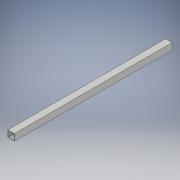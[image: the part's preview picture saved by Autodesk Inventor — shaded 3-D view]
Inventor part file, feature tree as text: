
AUTODESK INVENTOR PART (.ipt)
format: ipt  version: 2017 SP1 (Build 210196100, 196)  size: 98,304 bytes
history: native  units: in
note: dims shown in document units (in); Inventor stores cm internally (conversion verified against a paired STEP export)
features: extrude x1, sketch x1
ambient origin geometry x8: Origin, YZ Plane, XZ Plane, XY Plane, X Axis, Y Axis, Z Axis, Center Point
bodies: Solid1 (feature_tree)
feature tree (2):
  extrude  "Extrusion1"  Depth=1.0in
  sketch  "Sketch1"  dims[d0=1.0in d1=1.0in d2=0.0625in d3=24.0in d4=0.0in]
